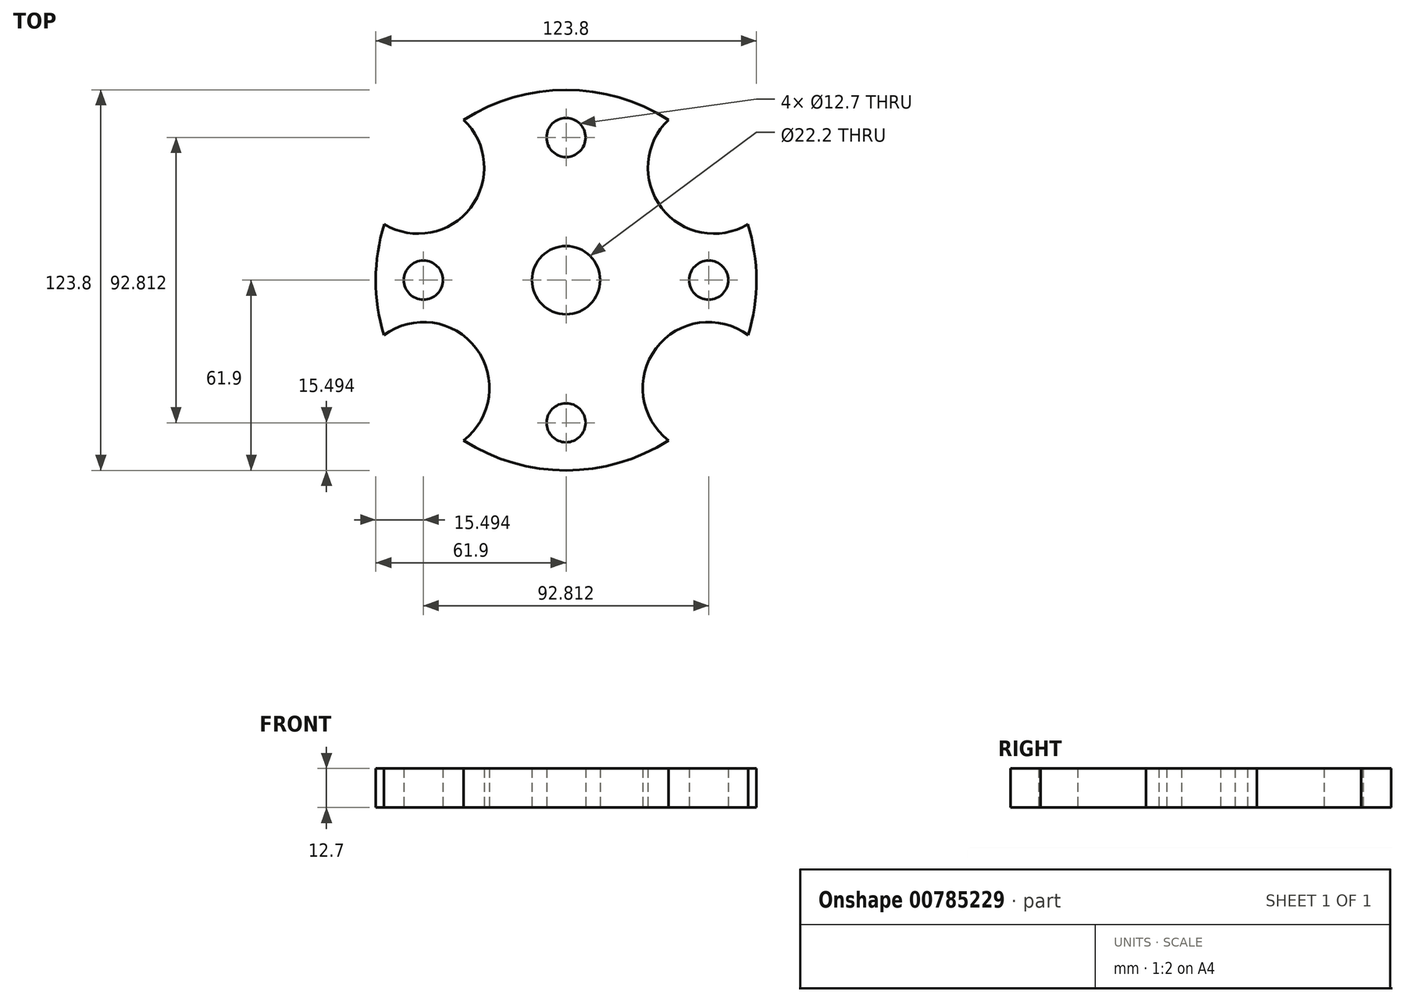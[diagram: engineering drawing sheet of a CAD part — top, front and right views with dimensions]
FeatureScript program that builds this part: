
annotation { "Feature Type Name" : "Feature", "Feature Type Description" : "" }
export const myFeature = defineFeature(function(context is Context, id is Id, definition is map)
    precondition{}
    {
        {
            var Q0;
            Q0=qCreatedBy(makeId("Top.planeOp"),FACE);
            var sketch = newSketch(context, id + "F0", { "sketchPlane" : qUnion([Q0])});
            skArc(sketch, "E0", {"start": v(-59.17, 18.18) * mm, "mid": v(-61.9, 0.13) * mm, "end": v(-59.25, -17.93) * mm});
            skCircle(sketch, "E1", {"center": v(0, 0) * mm, "radius": 11.1 * mm});
            skArc(sketch, "E2", {"start": v(33.34, 52.15) * mm, "mid": v(31.01, 23.58) * mm, "end": v(59.17, 18.18) * mm});
            skArc(sketch, "E3", {"start": v(59.25, -17.93) * mm, "mid": v(29.3, -22.18) * mm, "end": v(33.34, -52.15) * mm});
            skArc(sketch, "E4", {"start": v(-33.34, -52.15) * mm, "mid": v(-29.3, -22.18) * mm, "end": v(-59.25, -17.93) * mm});
            skArc(sketch, "E5", {"start": v(-59.17, 18.18) * mm, "mid": v(-31.01, 23.58) * mm, "end": v(-33.34, 52.15) * mm});
            skArc(sketch, "E6.trimOffspring", {"start": v(33.34, 52.15) * mm, "mid": v(0, 61.9) * mm, "end": v(-33.34, 52.15) * mm});
            skArc(sketch, "E7.trimOffspring", {"start": v(59.25, -17.93) * mm, "mid": v(61.9, 0.13) * mm, "end": v(59.17, 18.18) * mm});
            skArc(sketch, "E8.trimOffspring", {"start": v(-33.34, -52.15) * mm, "mid": v(0, -61.9) * mm, "end": v(33.34, -52.15) * mm});
            skLineSegment(sketch, "E9", {"start": v(-48.1, 36.57) * mm, "end": v(48.1, 36.57) * mm, "construction": true});
            skCircle(sketch, "E10", {"center": v(-46.4, 0) * mm, "radius": 6.35 * mm});
            skCircle(sketch, "E11", {"center": v(0, 46.4) * mm, "radius": 6.35 * mm});
            skCircle(sketch, "E12", {"center": v(46.4, 0) * mm, "radius": 6.35 * mm});
            skCircle(sketch, "E13", {"center": v(0, -46.4) * mm, "radius": 6.35 * mm});
            skSolve(sketch);
        }
        {
            var Q0;
            Q0=makeQuery(id+"F0.imprint","IMPRINT",FACE,{"disambiguationData":[TD([[makeQuery(id+"F0.imprint","IMPRINT",EDGE,{"derivedFrom":sQuery(id+"F0.wireOp",EDGE,"E0")}),1.0]])]});
            var sketch = newSketch(context, id + "F1", { "sketchPlane" : qUnion([Q0])});
            skSolve(sketch);
        }
        {
            var Q0;
            Q0=makeQuery(id+"F1.imprint","IMPRINT",FACE,{"disambiguationData":[TD([[makeQuery(id+"F1.imprint","IMPRINT",EDGE,{"derivedFrom":makeQuery(id+"F0.imprint","IMPRINT",EDGE,{"derivedFrom":sQuery(id+"F0.wireOp",EDGE,"E0")})}),1.0]])]});
            extrude(context, id + "F2", {"entities" : qUnion([Q0]), "depth" : 12.7 * mm, "offsetDistance" : 25.4 * mm});
        }
    });
